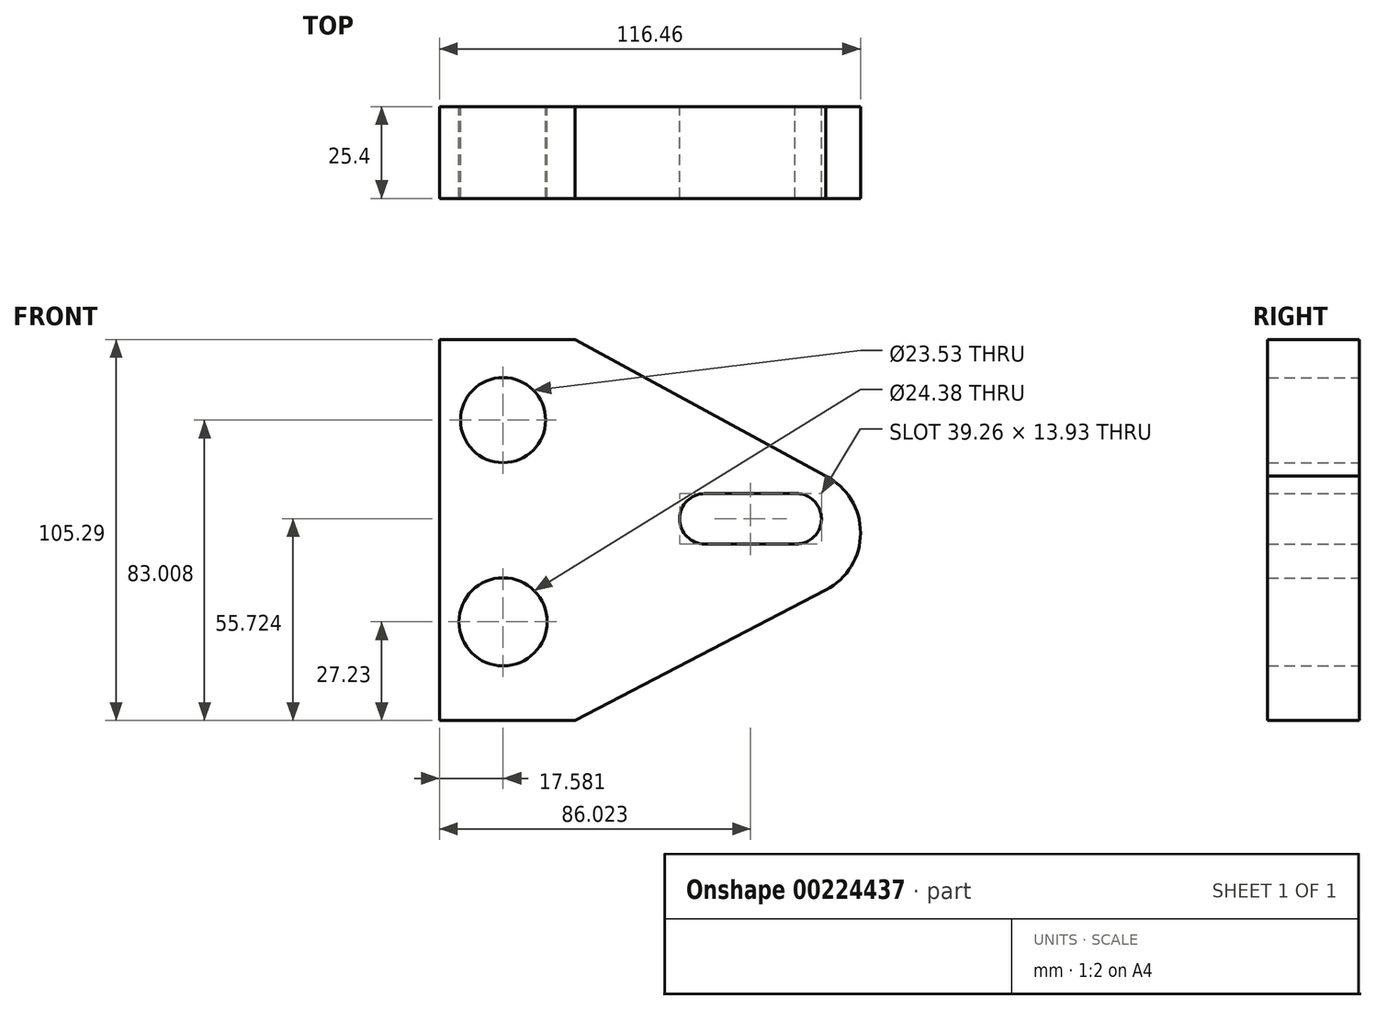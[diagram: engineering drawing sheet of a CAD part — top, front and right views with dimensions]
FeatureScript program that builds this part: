
annotation { "Feature Type Name" : "Feature", "Feature Type Description" : "" }
export const myFeature = defineFeature(function(context is Context, id is Id, definition is map)
    precondition{}
    {
        {
            var Q0;
            Q0=qCreatedBy(makeId("Front.planeOp"),FACE);
            var sketch = newSketch(context, id + "F0", { "sketchPlane" : qUnion([Q0])});
            skLineSegment(sketch, "E0", {"start": v(-60.5, 42.6) * mm, "end": v(-60.5, -62.7) * mm});
            skLineSegment(sketch, "E1", {"start": v(-60.5, 42.6) * mm, "end": v(-23.06, 42.6) * mm});
            skLineSegment(sketch, "E2", {"start": v(-60.5, -62.7) * mm, "end": v(-23.06, -62.7) * mm});
            skLineSegment(sketch, "E3", {"start": v(-23.06, -62.7) * mm, "end": v(46.37, -26.65) * mm});
            skLineSegment(sketch, "E4", {"start": v(-23.06, 42.6) * mm, "end": v(46.37, 4.9) * mm});
            skArc(sketch, "E5", {"start": v(46.37, -26.65) * mm, "mid": v(55.96, -10.87) * mm, "end": v(46.37, 4.9) * mm});
            skCircle(sketch, "E6", {"center": v(-42.92, 20.32) * mm, "radius": 11.77 * mm});
            skCircle(sketch, "E7", {"center": v(-42.92, -35.46) * mm, "radius": 12.19 * mm});
            skLineSegment(sketch, "E8", {"start": v(12.86, 0) * mm, "end": v(37.81, 0) * mm});
            skLineSegment(sketch, "E9", {"start": v(12.86, -13.93) * mm, "end": v(38.18, -13.93) * mm});
            skArc(sketch, "E10", {"start": v(12.86, 0) * mm, "mid": v(5.9, -6.97) * mm, "end": v(12.86, -13.93) * mm});
            skArc(sketch, "E11", {"start": v(38.18, -13.93) * mm, "mid": v(45.15, -6.77) * mm, "end": v(37.81, 0) * mm});
            skSolve(sketch);
        }
        {
            var Q0;
            Q0 = qSketchRegion(id + "F0", true);
            extrude(context, id + "F1", {"entities" : qUnion([Q0]), "depth" : 25.4 * mm});
        }
    });
